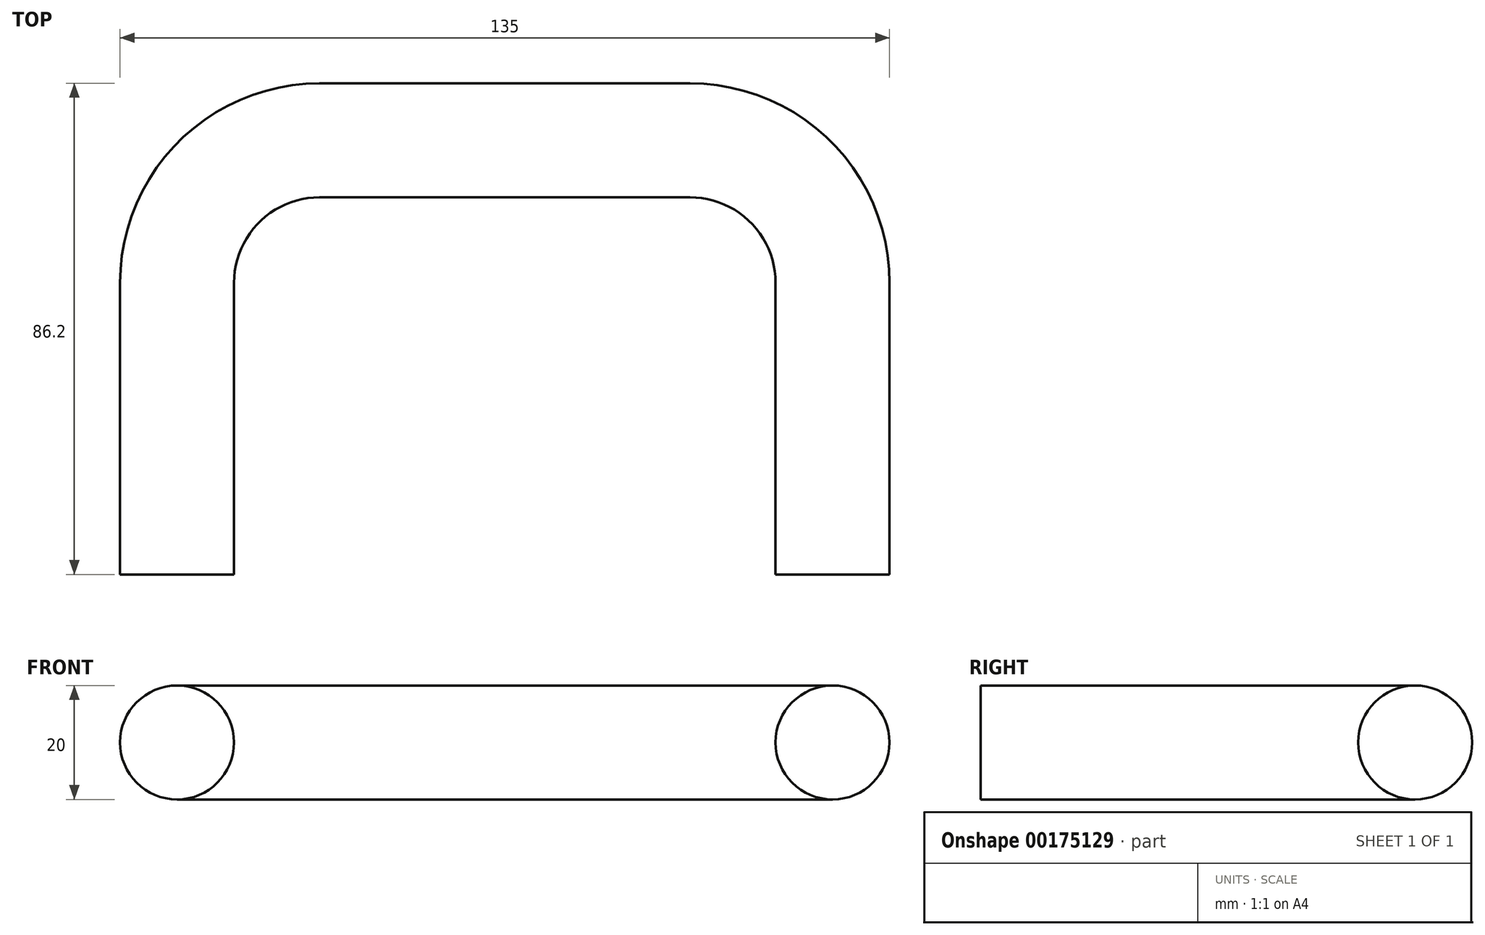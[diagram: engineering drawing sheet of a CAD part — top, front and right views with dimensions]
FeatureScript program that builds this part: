
annotation { "Feature Type Name" : "Feature", "Feature Type Description" : "" }
export const myFeature = defineFeature(function(context is Context, id is Id, definition is map)
    precondition{}
    {
        {
            var Q0;
            Q0=qCreatedBy(makeId("Top.planeOp"),FACE);
            var sketch = newSketch(context, id + "F0", { "sketchPlane" : qUnion([Q0])});
            skLineSegment(sketch, "E0", {"start": v(0, 0) * mm, "end": v(0, 51.2) * mm});
            skLineSegment(sketch, "E1", {"start": v(25, 76.2) * mm, "end": v(90, 76.2) * mm});
            skLineSegment(sketch, "E2", {"start": v(115, 51.2) * mm, "end": v(115, 0) * mm});
            skPoint(sketch, "E3.visualSharp", {"position": v(115, 76.2) * mm});
            skArc(sketch, "E3.filletArc", {"start": v(115, 51.2) * mm, "mid": v(107.68, 68.88) * mm, "end": v(90, 76.2) * mm});
            skPoint(sketch, "E4.visualSharp", {"position": v(0, 76.2) * mm});
            skArc(sketch, "E4.filletArc", {"start": v(25, 76.2) * mm, "mid": v(7.32, 68.88) * mm, "end": v(0, 51.2) * mm});
            skSolve(sketch);
        }
        {
            var Q0;
            Q0=qCreatedBy(makeId("Front.planeOp"),FACE);
            var sketch = newSketch(context, id + "F1", { "sketchPlane" : qUnion([Q0])});
            skCircle(sketch, "E5", {"center": v(0, 0) * mm, "radius": 10 * mm});
            skSolve(sketch);
        }
        {
            var Q0;
            Q0=makeQuery(id+"F1.imprint","IMPRINT",FACE,{"disambiguationData":[TD([[makeQuery(id+"F1.imprint","IMPRINT",EDGE,{"derivedFrom":sQuery(id+"F1.wireOp",EDGE,"E5")}),1.0]])]});
            var Q1;
            Q1=sQuery(id+"F1.wireOp",EDGE,"E5");
            var Q2;
            Q2=sQuery(id+"F0.wireOp",EDGE,"E0");
            var Q3;
            Q3=sQuery(id+"F0.wireOp",EDGE,"E1");
            var Q4;
            Q4=sQuery(id+"F0.wireOp",EDGE,"E2");
            var Q5;
            Q5=sQuery(id+"F0.wireOp",EDGE,"E4.filletArc");
            var Q6;
            Q6=sQuery(id+"F0.wireOp",EDGE,"E3.filletArc");
            sweep(context, id + "F2", {"profiles" : qUnion([Q0]), "surfaceProfiles" : qUnion([Q1]), "path" : qUnion([Q2, Q3, Q4, Q5, Q6])});
        }
    });
